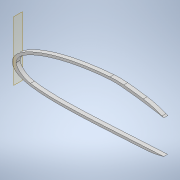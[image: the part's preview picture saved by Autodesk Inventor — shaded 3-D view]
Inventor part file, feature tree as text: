
AUTODESK INVENTOR PART (.ipt)
format: ipt  version: 2022.1 (Build 261234020, 234B)  size: 618,496 bytes
history: native  units: mm
features: sketch x8, extrude x7, projected_geometry x5, thicken_offset x4, fillet x4, shell x1, plane x1, other x1
ambient origin geometry x8: Origin, YZ Plane, XZ Plane, XY Plane, X Axis, Y Axis, Z Axis, Center Point
bodies: Solid1 (feature_tree)
feature tree (31):
  extrude  "Extrusion1"  Depth=3.0mm
  shell  "Shell1"  Thickness=1.0mm
  thicken_offset  "Thicken1"
  extrude  "Extrusion27"  TaperAngle=0.0deg  [1 undecoded]
  thicken_offset  "Thicken3"
  extrude  "Extrusion29"  Depth=20.0mm
  plane  "Work Plane5"
  other  "Bend Part2"
  thicken_offset  "Thicken5"
  extrude  "Extrusion30"  Depth=5.0mm TaperAngle=0.0deg
  fillet  "Fillet6"  Radius=10.0mm
  extrude  "Extrusion31"  Depth=1.0mm
  fillet  "Fillet7"  Radius=50.0mm
  extrude  "Extrusion32"  Depth=5.0mm TaperAngle=0.0deg
  fillet  "Fillet8"  Radius=500.0mm
  thicken_offset  "Thicken6"
  extrude  "Extrusion33"  Depth=60.0mm
  fillet  "Fillet9"  Radius=600.0mm
  sketch  "Sketch3"  dims[d0=5.0mm d1=0.0mm d2=3.0mm d159=1.0mm d160=2.0mm]
  sketch  "Sketch48"  dims[d236=190.0mm d237=0.0mm d238=0.0mm]
  sketch  "Sketch55"  dims[d249=2.0mm d250=1.0mm d254=20.0mm]
  projected_geometry  "Projected Loop32"
  sketch  "Sketch57"  dims[d255=8.0mm d256=5.0mm d257=0.0mm d262=10.0mm d263=0.174533mm]
  sketch  "Sketch58"  dims[d264=1.0mm d265=1.0mm d268=50.0mm]
  projected_geometry  "Projected Loop34"
  sketch  "Sketch59"  dims[d269=9.0mm d270=5.0mm d271=0.0mm d272=500.0mm]
  projected_geometry  "Projected Loop35"
  sketch  "Sketch60"  dims[d273=200.0mm d274=60.0mm d275=600.0mm]
  projected_geometry  "Projected Loop36"
  sketch  "Sketch61"  dims[d276=5.0mm d277=0.0mm d278=100.0mm d279=5.0mm d280=60.0mm d281=500.0mm d282=10.0mm d283=0.0mm d284=100.0mm d285=2.0mm d286=3.0mm d287=10.0mm d288=0.0mm d289=100.0mm]
  projected_geometry  "Projected Loop37"
note: 1 required parameter value undecoded (feature->parameter linkage not recoverable at this tier; creation-order binding heuristic only, values carry confidence <= 0.55)
